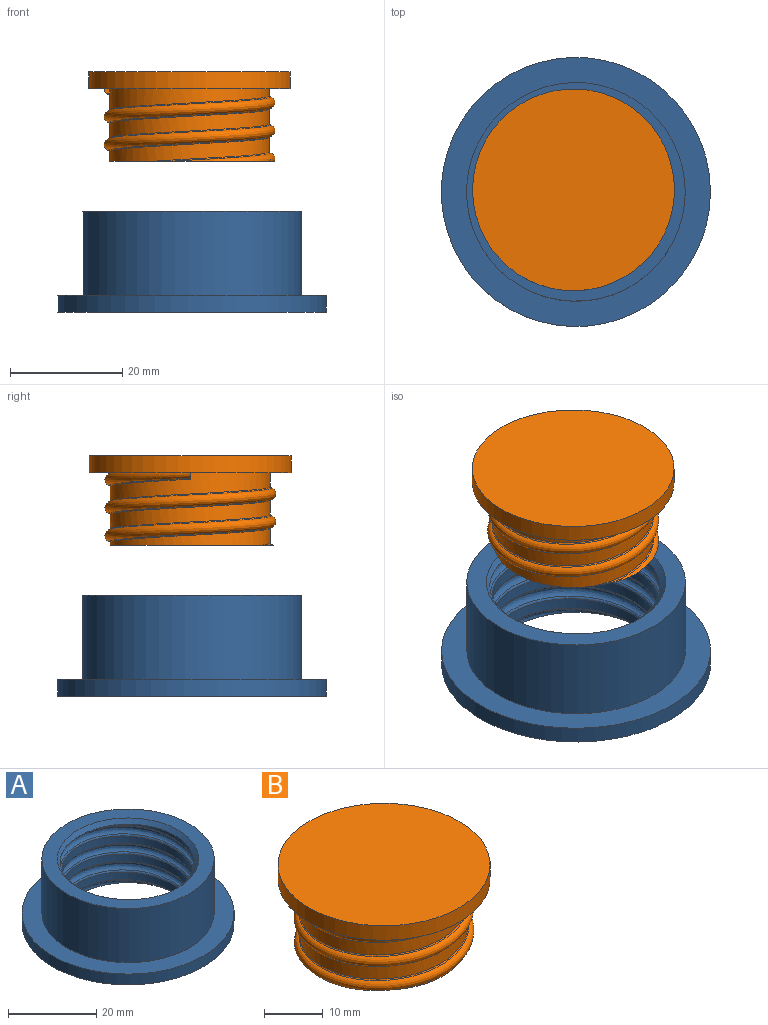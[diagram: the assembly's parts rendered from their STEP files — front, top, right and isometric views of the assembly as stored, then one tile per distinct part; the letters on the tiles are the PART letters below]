
ASSEMBLY  parts=2 mates=1
PART A: 11 faces, bbox 48.3x48.3x22.5 mm
  f0: cylinder r=15mm len=30mm, axis (0,0,1), area 637.3mm2, adj f7,f8,f9,f10
  f1: cylinder r=24mm len=48mm, axis (0,0,1), area 452.4mm2, adj f3,f6
  f2: bspline ~39.72x34.4mm, area 1004mm2, adj f5,f6,f7,f8,f9,f10
  f3: plane 48x48mm, normal (0,0,1), area 615mm2, adj f1,f4
  f4: cylinder r=19.5mm len=39mm, axis (0,0,-1), area 1837.8mm2, adj f3,f5
  f5: plane 39.26x39.26mm, normal (0,0,1), area 389.1mm2, adj f2,f4,f8
  f6: plane 48.29x48.29mm, normal (0,0,-1), area 1004.1mm2, adj f1,f2,f7
  f7: cone r=16mm half-angle=45deg, axis (0,0,-1), area 87.4mm2, adj f0,f2,f6,f9,f10
  f8: cone r=15mm half-angle=45deg, axis (0,0,1), area 87.4mm2, adj f0,f2,f5,f9,f10
  f9: bspline ~30.6x30.6mm, area 155.9mm2, adj f0,f2,f7,f8
  f10: bspline ~30.6x30.6mm, area 153.7mm2, adj f0,f2,f7,f8
PART B: 9 faces, bbox 36.7x38.2x18.9 mm
  f0: bspline ~37.53x32.5mm, area 674.1mm2, adj f1,f3,f4,f7,f8
  f1: plane 1.38x1.2mm, normal (0,1,0), area 0.8mm2, adj f0,f2,f4,f8
  f2: cylinder r=14.25mm len=28.5mm, axis (0,0,-1), area 632.4mm2, adj f1,f3,f4,f7,f8
  f3: plane 30.03x29.85mm, normal (0,0,-1), area 667.1mm2, adj f0,f2,f7,f8
  f4: plane 36.71x36.71mm, normal (0,0,-1), area 365.3mm2, adj f0,f1,f2,f5,f7
  f5: cylinder r=18mm len=36mm, axis (0,0,-1), area 339.3mm2, adj f4,f6
  f6: plane 36x36mm, normal (0,0,1), area 1017.9mm2, adj f5
  f7: bspline ~28.84x28.84mm, area 65.6mm2, adj f0,f2,f3,f4
  f8: bspline ~28.84x28.84mm, area 60.2mm2, adj f0,f1,f2,f3
PLACE A t=(-56.22,-33.05,15.76)mm
PLACE B rot(axis=(0,0,1),180deg) t=(-56.65,-32.75,37.66)mm
MATE cylindrical B.f3 <-> A.f0  axis (0,0,-1) through (-56.22,-33.05,39.66)mm
